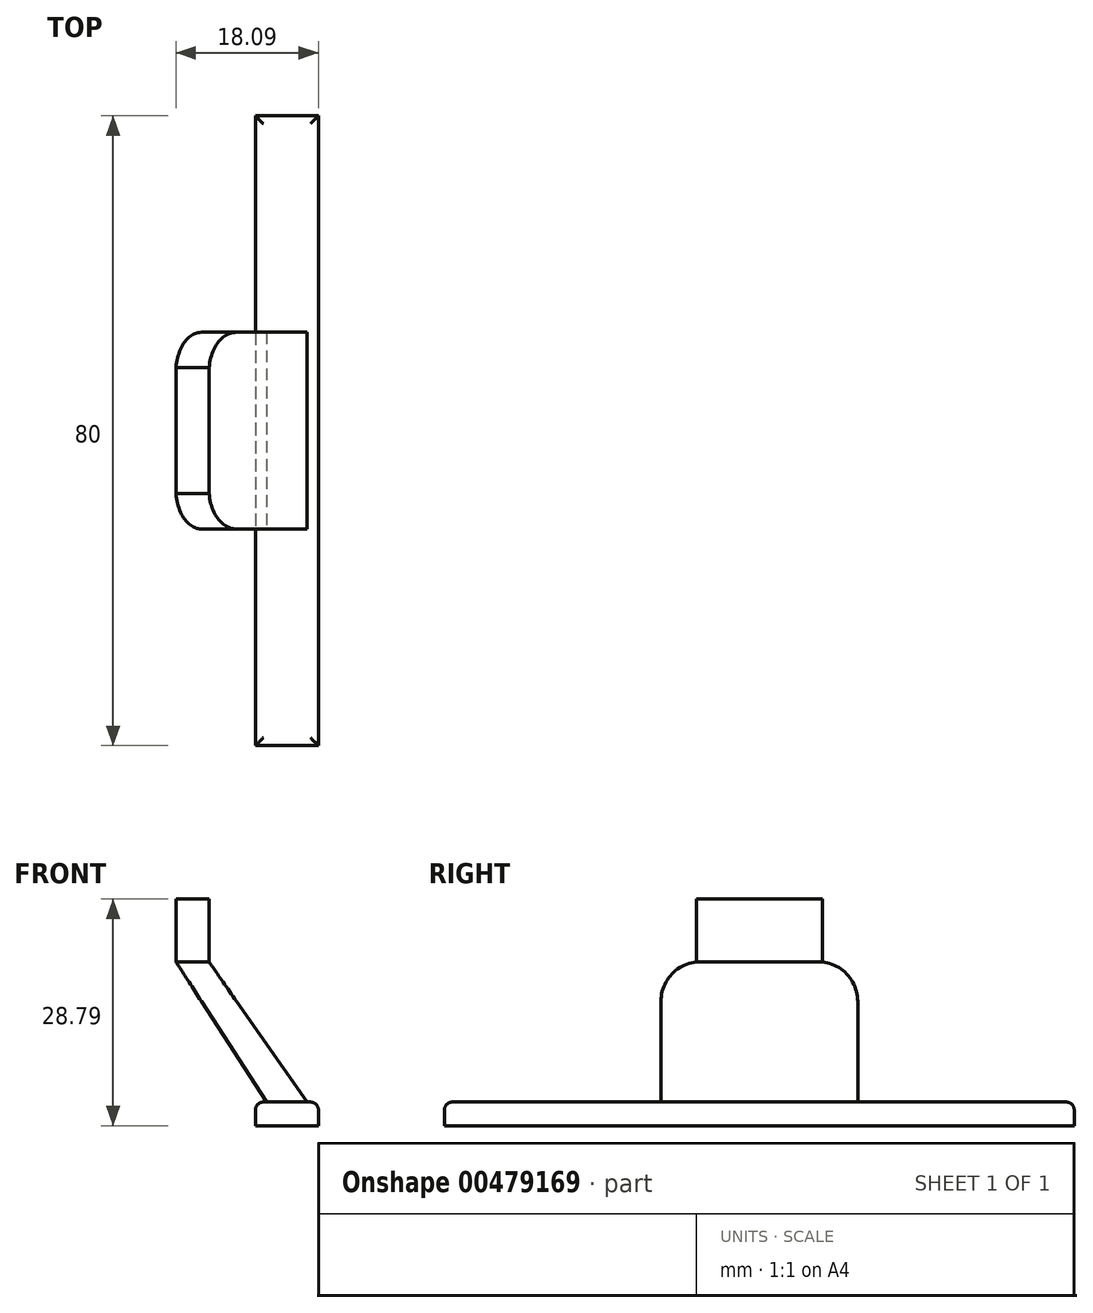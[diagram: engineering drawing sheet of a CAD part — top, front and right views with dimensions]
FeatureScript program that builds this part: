
annotation { "Feature Type Name" : "Feature", "Feature Type Description" : "" }
export const myFeature = defineFeature(function(context is Context, id is Id, definition is map)
    precondition{}
    {
        {
            var Q0;
            Q0=qCreatedBy(makeId("Top.planeOp"),FACE);
            var sketch = newSketch(context, id + "F0", { "sketchPlane" : qUnion([Q0])});
            skLineSegment(sketch, "E0.bottom", {"start": v(2.1, -8) * mm, "end": v(-2.1, -8) * mm});
            skLineSegment(sketch, "E0.top", {"start": v(2.1, 8) * mm, "end": v(-2.1, 8) * mm});
            skLineSegment(sketch, "E0.left", {"start": v(2.1, -8) * mm, "end": v(2.1, 8) * mm});
            skLineSegment(sketch, "E0.right", {"start": v(-2.1, -8) * mm, "end": v(-2.1, 8) * mm});
            skPoint(sketch, "E0.middle", {"position": v(0, 0) * mm});
            skSolve(sketch);
        }
        {
            var Q0;
            Q0=makeQuery(id+"F0.imprint","IMPRINT",FACE,{"disambiguationData":[TD([[makeQuery(id+"F0.imprint","IMPRINT",EDGE,{"derivedFrom":sQuery(id+"F0.wireOp",EDGE,"E0.bottom")}),-1.0]])]});
            extrude(context, id + "F1", {"entities" : qUnion([Q0]), "depth" : 8 * mm, "offsetDistance" : 25 * mm});
        }
        {
            var Q0;
            {var subQ0=sQuery(id+"F0.wireOp",EDGE,"E0.bottom");Q0=makeQuery(id+"F4.boolean.opBoolean","MERGE",FACE,{"derivedFrom":[makeQuery(id+"F1.opExtrude","SWEPT_FACE",FACE,{"disambiguationData":[OSD([subQ0])]}),makeQuery(id+"F4.opExtrude","CAP_FACE",FACE,{"disambiguationData":[OSD([subQ0,sQuery(id+"F3.wireOp",EDGE,"E1"),sQuery(id+"F3.wireOp",EDGE,"E3"),sQuery(id+"F3.wireOp",EDGE,"E4"),sQuery(id+"F3.wireOp",EDGE,"E5")])],"isStart":true})]});}
            cPlane(context, id + "F2", {"entities" : qUnion([Q0]), "cplaneType" : CPlaneType.OFFSET, "offset" : 8 * mm, "oppositeDirection" : true, "width" : 150 * mm, "height" : 150 * mm});
        }
        {
            var Q0;
            Q0=qCreatedBy(id+"F2.planeOp",FACE);
            var sketch = newSketch(context, id + "F3", { "sketchPlane" : qUnion([Q0])});
            skLineSegment(sketch, "E1", {"start": v(2.1, 0) * mm, "end": v(13.57, -16.38) * mm});
            skLineSegment(sketch, "E2", {"start": v(13.57, -16.38) * mm, "end": v(11.56, -17.8) * mm});
            skLineSegment(sketch, "E3", {"start": v(11.56, -17.8) * mm, "end": v(-0.9, 0) * mm});
            skLineSegment(sketch, "E4", {"start": v(13.57, -16.38) * mm, "end": v(14.56, -17.8) * mm});
            skLineSegment(sketch, "E5", {"start": v(14.56, -17.8) * mm, "end": v(11.56, -17.8) * mm});
            skLineSegment(sketch, "E6", {"start": v(-0.9, 0) * mm, "end": v(2.1, 0) * mm});
            skLineSegment(sketch, "E7.0", {"start": v(2.1, 0) * mm, "end": v(-2.1, 0) * mm});
            skLineSegment(sketch, "E8", {"start": v(-2.1, 0) * mm, "end": v(9.42, -17.8) * mm});
            skLineSegment(sketch, "E9", {"start": v(9.42, -17.8) * mm, "end": v(11.56, -17.8) * mm});
            skSolve(sketch);
        }
        {
            var Q0;
            Q0 = qSketchRegion(id + "F3", true);
            var Q1;
            {var subQ0=sQuery(id+"F3.wireOp",EDGE,"E1");Q1=makeQuery(id+"F3.imprint","IMPRINT",FACE,{"disambiguationData":[TD([[makeQuery(id+"F3.imprint","IMPRINT",EDGE,{"derivedFrom":subQ0}),-1.0]])]});}
            extrude(context, id + "F4", {"entities" : qUnion([Q0, Q1]), "operationType" : NewBodyOperationType.ADD, "endBound" : BoundingType.SYMMETRIC, "oppositeDirection" : true, "depth" : 25 * mm, "offsetDistance" : 25 * mm});
        }
        {
            var Q0;
            Q0=makeQuery(id+"F4.opExtrude","SWEPT_FACE",FACE,{"disambiguationData":[OSD([sQuery(id+"F3.wireOp",EDGE,"E5")])]});
            var sketch = newSketch(context, id + "F5", { "sketchPlane" : qUnion([Q0])});
            skLineSegment(sketch, "E10.0", {"start": v(9.42, -12.5) * mm, "end": v(9.42, 12.5) * mm, "construction": true});
            skLineSegment(sketch, "E11.0", {"start": v(14.56, -12.5) * mm, "end": v(14.56, 12.5) * mm, "construction": true});
            skLineSegment(sketch, "E12", {"start": v(9.42, 0) * mm, "end": v(14.56, 0) * mm, "construction": true});
            skLineSegment(sketch, "E13", {"start": v(14.56, 0) * mm, "end": v(11.99, 0) * mm, "construction": true});
            skLineSegment(sketch, "E14", {"start": v(11.99, 0) * mm, "end": v(11.99, 12.5) * mm, "construction": true});
            skLineSegment(sketch, "E15.bottom", {"start": v(15.99, -40) * mm, "end": v(7.99, -40) * mm});
            skLineSegment(sketch, "E15.top", {"start": v(15.99, 40) * mm, "end": v(7.99, 40) * mm});
            skLineSegment(sketch, "E15.left", {"start": v(15.99, -40) * mm, "end": v(15.99, 40) * mm});
            skLineSegment(sketch, "E15.right", {"start": v(7.99, -40) * mm, "end": v(7.99, 40) * mm});
            skPoint(sketch, "E15.middle", {"position": v(11.99, 0) * mm});
            skSolve(sketch);
        }
        {
            var Q0;
            Q0 = qSketchRegion(id + "F5", true);
            extrude(context, id + "F6", {"entities" : qUnion([Q0]), "operationType" : NewBodyOperationType.ADD, "depth" : 3 * mm, "offsetDistance" : 25 * mm});
        }
        {
            var Q0;
            Q0=makeQuery(id+"F6.opExtrude","CAP_EDGE",EDGE,{"disambiguationData":[OSD([sQuery(id+"F5.wireOp",EDGE,"E15.left")])],"isStart":true});
            var Q1;
            Q1=makeQuery(id+"F6.opExtrude","CAP_EDGE",EDGE,{"disambiguationData":[OSD([sQuery(id+"F5.wireOp",EDGE,"E15.bottom")])],"isStart":true});
            var Q2;
            Q2=makeQuery(id+"F6.opExtrude","CAP_EDGE",EDGE,{"disambiguationData":[OSD([sQuery(id+"F5.wireOp",EDGE,"E15.right")])],"isStart":true});
            var Q3;
            Q3=makeQuery(id+"F6.opExtrude","CAP_EDGE",EDGE,{"disambiguationData":[OSD([sQuery(id+"F5.wireOp",EDGE,"E15.top")])],"isStart":true});
            fillet(context, id + "F7", {"entities" : qUnion([Q0, Q1, Q2, Q3]), "radius" : 1 * mm, "tangentPropagation" : true, "allowEdgeOverflow" : false});
        }
        {
            var Q0;
            Q0=makeQuery(id+"F4.opExtrude","CAP_EDGE",EDGE,{"disambiguationData":[OSD([sQuery(id+"F3.wireOp",EDGE,"E7.0")])],"isStart":true});
            var Q1;
            Q1=makeQuery(id+"F4.opExtrude","CAP_EDGE",EDGE,{"disambiguationData":[OSD([sQuery(id+"F3.wireOp",EDGE,"E7.0")])],"isStart":false});
            fillet(context, id + "F8", {"entities" : qUnion([Q0, Q1]), "radius" : 5 * mm, "tangentPropagation" : true, "allowEdgeOverflow" : false});
        }
    });
